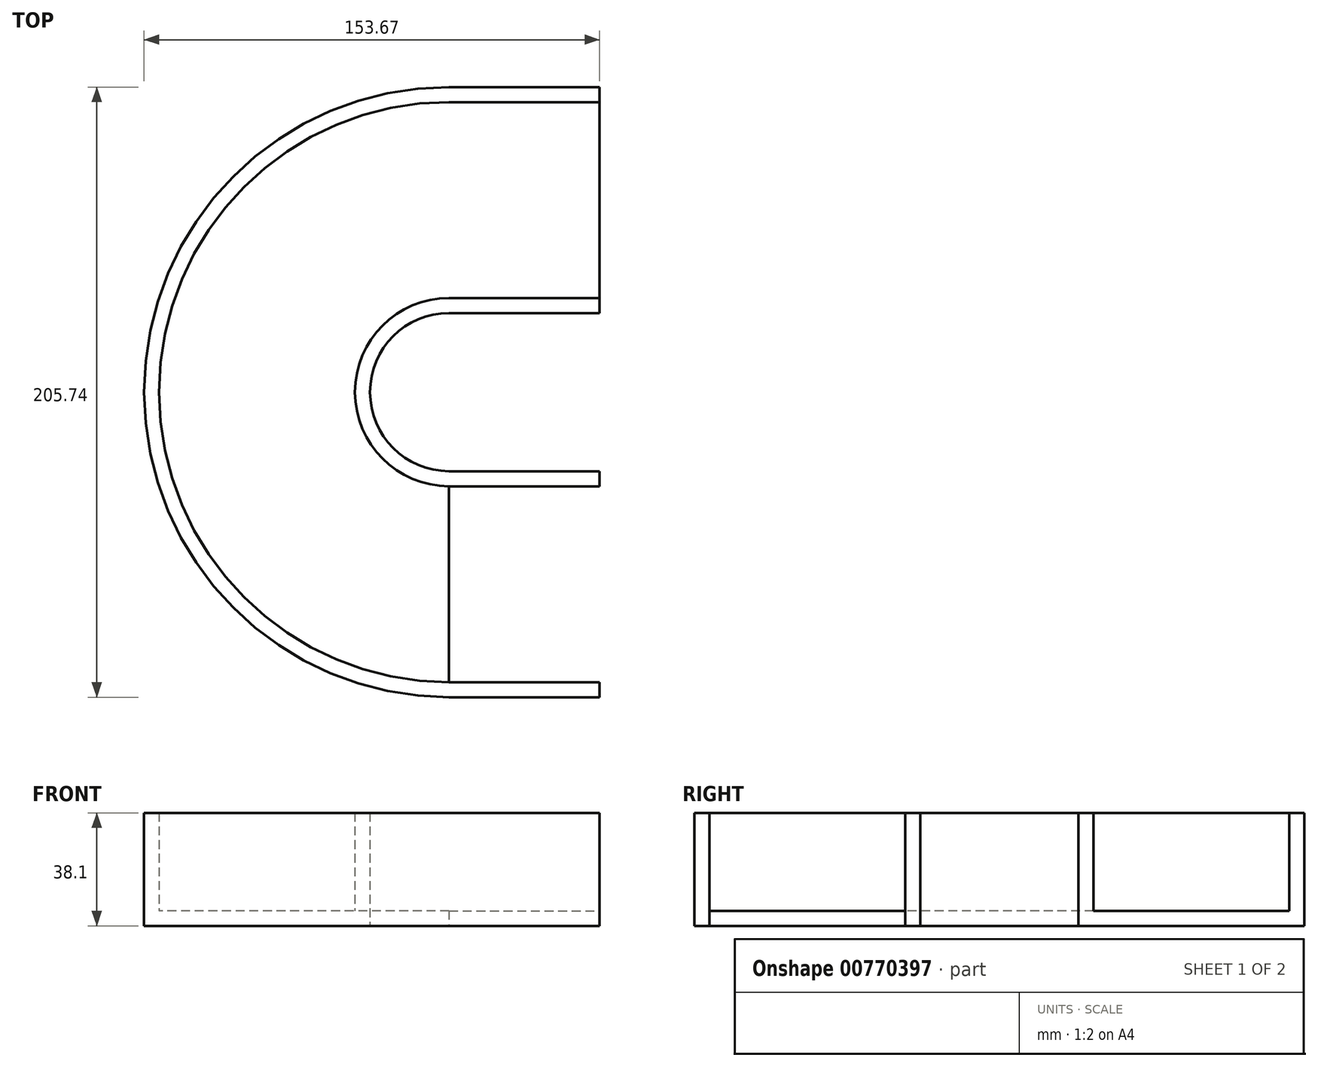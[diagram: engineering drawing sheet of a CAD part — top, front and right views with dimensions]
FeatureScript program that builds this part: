
annotation { "Feature Type Name" : "Feature", "Feature Type Description" : "" }
export const myFeature = defineFeature(function(context is Context, id is Id, definition is map)
    precondition{}
    {
        {
            var Q0;
            Q0=qCreatedBy(makeId("Top.planeOp"),FACE);
            var sketch = newSketch(context, id + "F0", { "sketchPlane" : qUnion([Q0])});
            skArc(sketch, "E0", {"start": v(0, 31.75) * mm, "mid": v(-31.75, 0) * mm, "end": v(0, -31.75) * mm});
            skArc(sketch, "E1", {"start": v(0, 102.87) * mm, "mid": v(-102.87, 0) * mm, "end": v(0, -102.87) * mm});
            skArc(sketch, "E2", {"start": v(0, 97.8) * mm, "mid": v(-97.8, 0) * mm, "end": v(0, -97.8) * mm});
            skLineSegment(sketch, "E3", {"start": v(0, 31.75) * mm, "end": v(50.8, 31.75) * mm});
            skLineSegment(sketch, "E4", {"start": v(0, -102.87) * mm, "end": v(50.8, -102.87) * mm});
            skLineSegment(sketch, "E5", {"start": v(0, -97.79) * mm, "end": v(50.8, -97.79) * mm});
            skLineSegment(sketch, "E6", {"start": v(0, -31.75) * mm, "end": v(50.8, -31.75) * mm});
            skLineSegment(sketch, "E7", {"start": v(50.8, -102.87) * mm, "end": v(50.8, -97.79) * mm});
            skLineSegment(sketch, "E8", {"start": v(50.8, 31.75) * mm, "end": v(50.8, 31.75) * mm});
            skLineSegment(sketch, "E9", {"start": v(50.8, -97.79) * mm, "end": v(50.8, -31.75) * mm});
            skLineSegment(sketch, "E10", {"start": v(50.8, -97.79) * mm, "end": v(0, -97.79) * mm});
            skLineSegment(sketch, "E11", {"start": v(50.8, 31.75) * mm, "end": v(50.8, 97.8) * mm});
            skLineSegment(sketch, "E12", {"start": v(0, 97.8) * mm, "end": v(50.8, 97.8) * mm});
            skLineSegment(sketch, "E13", {"start": v(50.8, 97.8) * mm, "end": v(50.8, 102.87) * mm});
            skLineSegment(sketch, "E14", {"start": v(50.8, 102.87) * mm, "end": v(0, 102.87) * mm});
            skArc(sketch, "E15", {"start": v(0, 26.67) * mm, "mid": v(-26.67, 0) * mm, "end": v(0, -26.67) * mm});
            skLineSegment(sketch, "E16", {"start": v(50.8, -31.75) * mm, "end": v(50.8, -26.67) * mm});
            skLineSegment(sketch, "E17", {"start": v(50.8, -26.67) * mm, "end": v(0, -26.67) * mm});
            skLineSegment(sketch, "E18", {"start": v(0, 26.67) * mm, "end": v(50.8, 26.67) * mm});
            skLineSegment(sketch, "E19", {"start": v(50.8, 26.67) * mm, "end": v(50.8, 31.75) * mm});
            skLineSegment(sketch, "E20", {"start": v(0, -102.87) * mm, "end": v(0, -97.8) * mm});
            skLineSegment(sketch, "E21", {"start": v(0, -97.8) * mm, "end": v(0, -31.75) * mm});
            skLineSegment(sketch, "E22", {"start": v(0, -31.75) * mm, "end": v(0, -26.67) * mm});
            skLineSegment(sketch, "E23", {"start": v(0, 26.67) * mm, "end": v(0, 31.75) * mm});
            skLineSegment(sketch, "E24", {"start": v(0, 31.75) * mm, "end": v(0, 97.8) * mm});
            skLineSegment(sketch, "E25", {"start": v(0, 97.8) * mm, "end": v(0, 102.87) * mm});
            skSolve(sketch);
        }
        {
            var Q0;
            Q0=makeQuery(id+"F0.imprint","IMPRINT",FACE,{"disambiguationData":[TD([[makeQuery(id+"F0.imprint","IMPRINT",EDGE,{"derivedFrom":sQuery(id+"F0.wireOp",EDGE,"E2")}),1.0]])]});
            var Q1;
            Q1=makeQuery(id+"F0.imprint","IMPRINT",FACE,{"disambiguationData":[TD([[makeQuery(id+"F0.imprint","IMPRINT",EDGE,{"derivedFrom":sQuery(id+"F0.wireOp",EDGE,"E10")}),-1.0]])]});
            var Q2;
            Q2=makeQuery(id+"F0.imprint","IMPRINT",FACE,{"disambiguationData":[TD([[makeQuery(id+"F0.imprint","IMPRINT",EDGE,{"derivedFrom":sQuery(id+"F0.wireOp",EDGE,"E3")}),1.0]])]});
            extrude(context, id + "F1", {"entities" : qUnion([Q0, Q1, Q2]), "depth" : 5.08 * mm, "offsetDistance" : 25.4 * mm});
        }
        {
            var Q0;
            Q0=makeQuery(id+"F0.imprint","IMPRINT",FACE,{"disambiguationData":[TD([[makeQuery(id+"F0.imprint","IMPRINT",EDGE,{"derivedFrom":sQuery(id+"F0.wireOp",EDGE,"E1")}),1.0]])]});
            var Q1;
            Q1=makeQuery(id+"F0.imprint","IMPRINT",FACE,{"disambiguationData":[TD([[makeQuery(id+"F0.imprint","IMPRINT",EDGE,{"derivedFrom":sQuery(id+"F0.wireOp",EDGE,"E4")}),1.0]])]});
            var Q2;
            Q2=makeQuery(id+"F0.imprint","IMPRINT",FACE,{"disambiguationData":[TD([[makeQuery(id+"F0.imprint","IMPRINT",EDGE,{"derivedFrom":sQuery(id+"F0.wireOp",EDGE,"E0")}),1.0]])]});
            var Q3;
            Q3=makeQuery(id+"F0.imprint","IMPRINT",FACE,{"disambiguationData":[TD([[makeQuery(id+"F0.imprint","IMPRINT",EDGE,{"derivedFrom":sQuery(id+"F0.wireOp",EDGE,"E6")}),1.0]])]});
            var Q4;
            Q4=makeQuery(id+"F0.imprint","IMPRINT",FACE,{"disambiguationData":[TD([[makeQuery(id+"F0.imprint","IMPRINT",EDGE,{"derivedFrom":sQuery(id+"F0.wireOp",EDGE,"E3")}),-1.0]])]});
            var Q5;
            Q5=makeQuery(id+"F0.imprint","IMPRINT",FACE,{"disambiguationData":[TD([[makeQuery(id+"F0.imprint","IMPRINT",EDGE,{"derivedFrom":sQuery(id+"F0.wireOp",EDGE,"E12")}),1.0]])]});
            extrude(context, id + "F2", {"entities" : qUnion([Q0, Q1, Q2, Q3, Q4, Q5]), "operationType" : NewBodyOperationType.ADD, "depth" : 38.1 * mm, "offsetDistance" : 25.4 * mm});
        }
    });
